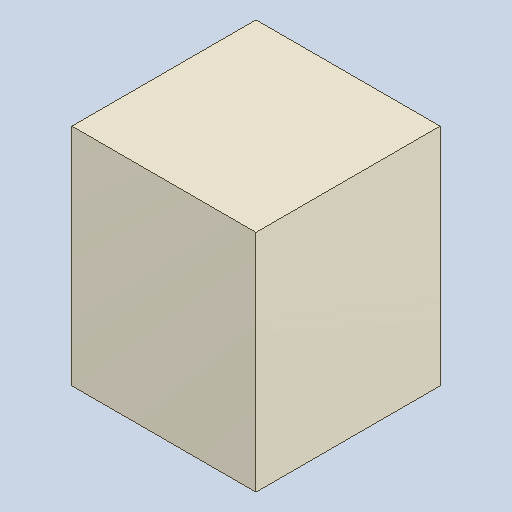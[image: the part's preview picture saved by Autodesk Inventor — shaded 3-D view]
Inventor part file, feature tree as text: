
AUTODESK INVENTOR PART (.ipt)
format: ipt  version: 2023.4 (Build 274418000, 418)  size: 82,944 bytes
history: native  units: mm
features: extrude x1
ambient origin geometry x8: Origin, YZ Plane, XZ Plane, XY Plane, X Axis, Y Axis, Z Axis, Center Point
bodies: Solid1 (feature_tree)
feature tree (1):
  extrude  "Extruded_15"  [1 undecoded]
note: 1 required parameter value undecoded (feature->parameter linkage not recoverable at this tier; creation-order binding heuristic only, values carry confidence <= 0.55)
